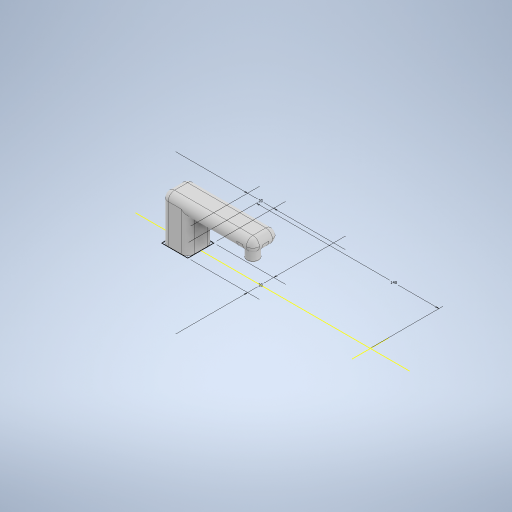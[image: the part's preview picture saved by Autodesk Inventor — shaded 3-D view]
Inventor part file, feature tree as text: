
AUTODESK INVENTOR PART (.ipt)
format: ipt  version: 2024.2 (Build 282272000, 272)  size: 325,632 bytes
history: native  units: mm
features: sketch x3, extrude x3, fillet x2, other x1
ambient origin geometry x8: Origin, YZ Plane, XZ Plane, XY Plane, X Axis, Y Axis, Z Axis, Center Point
bodies: Body1 (feature_tree)
feature tree (9):
  other  "Bryła1"
  sketch  "Szkic1"
  extrude  "Wyciągnięcie proste1"  Depth=20.0mm
  extrude  "Wyciągnięcie proste2"  Depth=20.0mm
  extrude  "Wyciągnięcie proste3"  Depth=140.0mm
  fillet  "Zaokrąglenie1"  Radius=35.0mm
  fillet  "Zaokrąglenie2"  Radius=20.0mm
  sketch  "Szkic2"
  sketch  "Szkic3"
